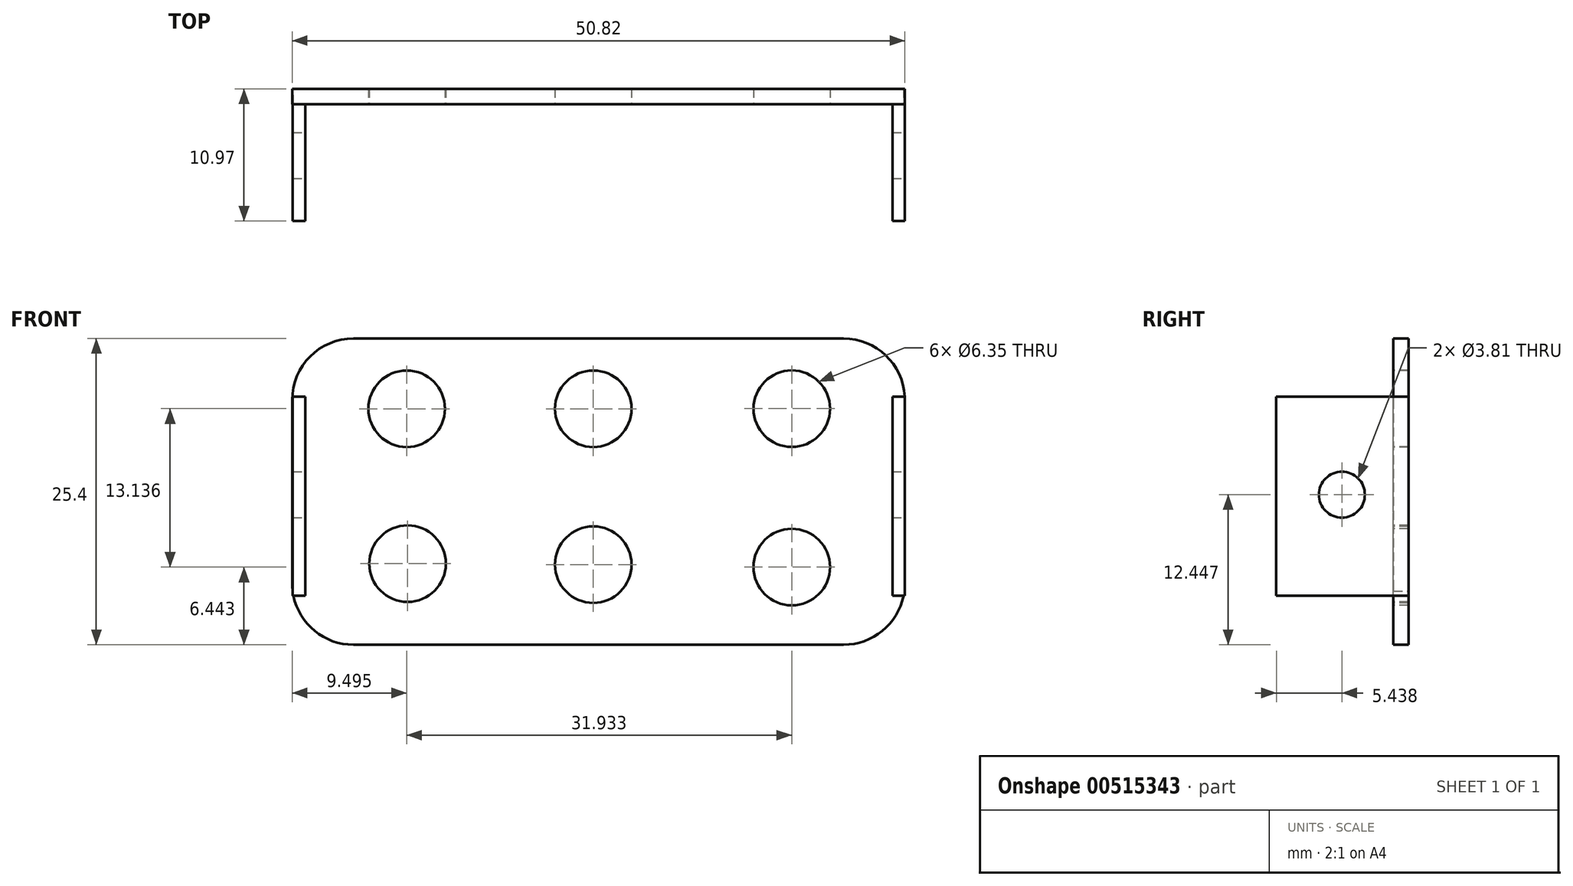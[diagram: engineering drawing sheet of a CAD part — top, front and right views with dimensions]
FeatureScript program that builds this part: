
annotation { "Feature Type Name" : "Feature", "Feature Type Description" : "" }
export const myFeature = defineFeature(function(context is Context, id is Id, definition is map)
    precondition{}
    {
        {
            var Q0;
            Q0=qCreatedBy(makeId("Front.planeOp"),FACE);
            var sketch = newSketch(context, id + "F0", { "sketchPlane" : qUnion([Q0])});
            skLineSegment(sketch, "E0.bottom", {"start": v(-24.97, 12.22) * mm, "end": v(25.83, 12.22) * mm});
            skLineSegment(sketch, "E0.top", {"start": v(-24.97, -13.18) * mm, "end": v(25.83, -13.18) * mm});
            skLineSegment(sketch, "E0.left", {"start": v(-24.97, 12.22) * mm, "end": v(-24.97, -13.18) * mm});
            skLineSegment(sketch, "E0.right", {"start": v(25.83, 12.22) * mm, "end": v(25.83, -13.18) * mm});
            skSolve(sketch);
        }
        {
            var Q0;
            Q0=makeQuery(id+"F0.imprint","IMPRINT",FACE,{"disambiguationData":[TD([[makeQuery(id+"F0.imprint","IMPRINT",EDGE,{"derivedFrom":sQuery(id+"F0.wireOp",EDGE,"E0.bottom")}),-1.0]])]});
            extrude(context, id + "F1", {"entities" : qUnion([Q0]), "depth" : 1.27 * mm, "offsetDistance" : 25.4 * mm});
        }
        {
            var Q0;
            Q0=makeQuery(id+"F1.opExtrude","CAP_FACE",FACE,{"disambiguationData":[OSD([sQuery(id+"F0.wireOp",EDGE,"E0.bottom"),sQuery(id+"F0.wireOp",EDGE,"E0.top"),sQuery(id+"F0.wireOp",EDGE,"E0.left"),sQuery(id+"F0.wireOp",EDGE,"E0.right")])],"isStart":false});
            var sketch = newSketch(context, id + "F2", { "sketchPlane" : qUnion([Q0])});
            skCircle(sketch, "E1", {"center": v(0, 6.4) * mm, "radius": 3.18 * mm});
            skCircle(sketch, "E2", {"center": v(0, -6.53) * mm, "radius": 3.18 * mm});
            skCircle(sketch, "E3", {"center": v(16.46, 6.4) * mm, "radius": 3.18 * mm});
            skCircle(sketch, "E4", {"center": v(16.46, -6.74) * mm, "radius": 3.18 * mm});
            skCircle(sketch, "E5", {"center": v(-15.4, -6.46) * mm, "radius": 3.18 * mm});
            skCircle(sketch, "E6", {"center": v(-15.47, 6.4) * mm, "radius": 3.17 * mm});
            skSolve(sketch);
        }
        {
            var Q0;
            Q0=sQuery(id+"F2.wireOp",VERTEX,"E2.center");
            var Q1;
            Q1=sQuery(id+"F2.wireOp",VERTEX,"E3.center");
            var Q2;
            Q2=sQuery(id+"F2.wireOp",VERTEX,"E1.center");
            var Q3;
            Q3=sQuery(id+"F2.wireOp",VERTEX,"E4.center");
            var Q4;
            Q4=sQuery(id+"F2.wireOp",VERTEX,"E5.center");
            var Q5;
            Q5=sQuery(id+"F2.wireOp",VERTEX,"E6.center");
            var Q6;
            Q6=makeQuery(id+"F1.opExtrude","SWEPT_BODY",BODY,{"disambiguationData":[OSD([sQuery(id+"F0.wireOp",EDGE,"E0.bottom"),sQuery(id+"F0.wireOp",EDGE,"E0.top"),sQuery(id+"F0.wireOp",EDGE,"E0.left"),sQuery(id+"F0.wireOp",EDGE,"E0.right")])]});
            hole(context, id + "F3", {"style" : HoleStyle.SIMPLE, "endStyle" : HoleEndStyle.THROUGH, "holeDiameter" : 6.35 * mm, "isTappedThrough" : true, "tappedDepth" : 12.7 * mm, "tapClearance" : 3, "locations" : qUnion([Q0, Q1, Q2, Q3, Q4, Q5]), "scope" : qUnion([Q6])});
        }
        {
            var Q0;
            Q0=makeQuery(id+"F1.opExtrude","SWEPT_EDGE",EDGE,{"disambiguationData":[OSD([sQuery(id+"F0.wireOp",EDGE,"E0.bottom"),sQuery(id+"F0.wireOp",EDGE,"E0.right")])]});
            var Q1;
            Q1=makeQuery(id+"F1.opExtrude","SWEPT_EDGE",EDGE,{"disambiguationData":[OSD([sQuery(id+"F0.wireOp",EDGE,"E0.top"),sQuery(id+"F0.wireOp",EDGE,"E0.right")])]});
            var Q2;
            Q2=makeQuery(id+"F1.opExtrude","SWEPT_EDGE",EDGE,{"disambiguationData":[OSD([sQuery(id+"F0.wireOp",EDGE,"E0.bottom"),sQuery(id+"F0.wireOp",EDGE,"E0.left")])]});
            var Q3;
            Q3=makeQuery(id+"F1.opExtrude","SWEPT_EDGE",EDGE,{"disambiguationData":[OSD([sQuery(id+"F0.wireOp",EDGE,"E0.top"),sQuery(id+"F0.wireOp",EDGE,"E0.left")])]});
            fillet(context, id + "F4", {"entities" : qUnion([Q0, Q1, Q2, Q3]), "radius" : 5.08 * mm, "tangentPropagation" : true, "allowEdgeOverflow" : false});
        }
        {
            var Q0;
            Q0=qCreatedBy(makeId("Front.planeOp"),FACE);
            var sketch = newSketch(context, id + "F5", { "sketchPlane" : qUnion([Q0])});
            skLineSegment(sketch, "E7.bottom", {"start": v(24.8, 7.4) * mm, "end": v(25.85, 7.4) * mm});
            skLineSegment(sketch, "E7.top", {"start": v(24.8, -9.1) * mm, "end": v(25.85, -9.1) * mm});
            skLineSegment(sketch, "E7.left", {"start": v(24.8, 7.4) * mm, "end": v(24.8, -9.1) * mm});
            skLineSegment(sketch, "E7.right", {"start": v(25.85, 7.4) * mm, "end": v(25.85, -9.1) * mm});
            skLineSegment(sketch, "E8.bottom", {"start": v(-23.89, 7.4) * mm, "end": v(-24.93, 7.4) * mm});
            skLineSegment(sketch, "E8.top", {"start": v(-23.89, -9.1) * mm, "end": v(-24.93, -9.1) * mm});
            skLineSegment(sketch, "E8.left", {"start": v(-23.89, 7.4) * mm, "end": v(-23.89, -9.1) * mm});
            skLineSegment(sketch, "E8.right", {"start": v(-24.93, 7.4) * mm, "end": v(-24.93, -9.1) * mm});
            skSolve(sketch);
        }
        {
            var Q0;
            Q0 = qSketchRegion(id + "F5", true);
            extrude(context, id + "F6", {"entities" : qUnion([Q0]), "operationType" : NewBodyOperationType.ADD, "depth" : 10.97 * mm, "offsetDistance" : 25.4 * mm});
        }
        {
            var Q0;
            Q0 = qSketchRegion(id + "F5", true);
            extrude(context, id + "F7", {"entities" : qUnion([Q0]), "operationType" : NewBodyOperationType.ADD, "depth" : 0.25 * mm, "offsetDistance" : 25.4 * mm});
        }
        {
            var Q0;
            Q0=makeQuery(id+"F6.opExtrude","SWEPT_FACE",FACE,{"disambiguationData":[OSD([sQuery(id+"F5.wireOp",EDGE,"E7.right")])]});
            var sketch = newSketch(context, id + "F8", { "sketchPlane" : qUnion([Q0])});
            skCircle(sketch, "E9", {"center": v(-5.53, -0.73) * mm, "radius": 2.75 * mm});
            skCircle(sketch, "E10", {"center": v(-5.53, -0.73) * mm, "radius": 1.02 * mm});
            skSolve(sketch);
        }
        {
            var Q0;
            Q0=sQuery(id+"F8.wireOp",VERTEX,"E9.center");
            var Q1;
            Q1=makeQuery(id+"F1.opExtrude","SWEPT_BODY",BODY,{"disambiguationData":[OSD([sQuery(id+"F0.wireOp",EDGE,"E0.bottom"),sQuery(id+"F0.wireOp",EDGE,"E0.top"),sQuery(id+"F0.wireOp",EDGE,"E0.left"),sQuery(id+"F0.wireOp",EDGE,"E0.right")])]});
            hole(context, id + "F9", {"style" : HoleStyle.SIMPLE, "endStyle" : HoleEndStyle.THROUGH, "holeDiameter" : 3.8 * mm, "isTappedThrough" : true, "tappedDepth" : 12.7 * mm, "tapClearance" : 3, "locations" : qUnion([Q0]), "scope" : qUnion([Q1])});
        }
    });
